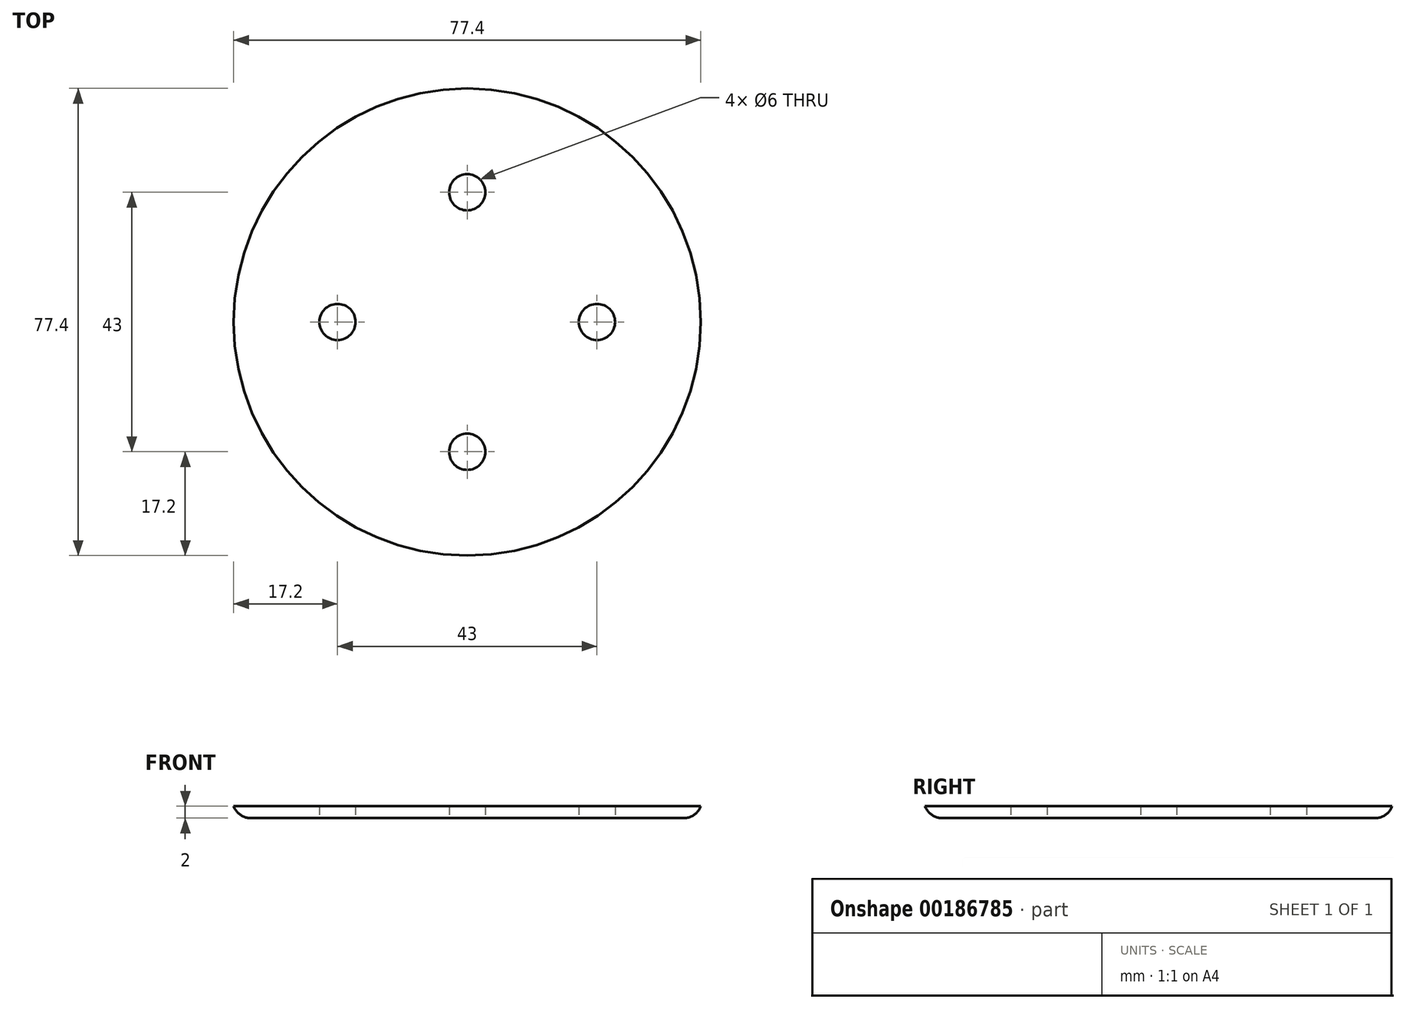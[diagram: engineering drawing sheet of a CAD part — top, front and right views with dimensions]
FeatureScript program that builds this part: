
annotation { "Feature Type Name" : "Feature", "Feature Type Description" : "" }
export const myFeature = defineFeature(function(context is Context, id is Id, definition is map)
    precondition{}
    {
        {
            var Q0;
            Q0=qCreatedBy(makeId("Top.planeOp"),FACE);
            var sketch = newSketch(context, id + "F0", { "sketchPlane" : qUnion([Q0])});
            skCircle(sketch, "E0", {"center": v(0, 0) * mm, "radius": 38.7 * mm});
            skLineSegment(sketch, "E1", {"start": v(-38.7, 0) * mm, "end": v(38.7, 0) * mm, "construction": true});
            skLineSegment(sketch, "E2", {"start": v(0, -38.7) * mm, "end": v(0, 38.7) * mm, "construction": true});
            skCircle(sketch, "E3", {"center": v(0, 21.5) * mm, "radius": 3 * mm});
            skCircle(sketch, "E4", {"center": v(21.5, 0) * mm, "radius": 3 * mm});
            skCircle(sketch, "E5", {"center": v(0, -21.5) * mm, "radius": 3 * mm});
            skCircle(sketch, "E6", {"center": v(-21.5, 0) * mm, "radius": 3 * mm});
            skSolve(sketch);
        }
        {
            var Q0;
            Q0 = qSketchRegion(id + "F0", true);
            extrude(context, id + "F1", {"entities" : qUnion([Q0]), "depth" : 2 * mm, "offsetDistance" : 25 * mm});
        }
        {
            var Q0;
            Q0=makeQuery(id+"F1.opExtrude","CAP_EDGE",EDGE,{"disambiguationData":[OSD([sQuery(id+"F0.wireOp",EDGE,"E0")])],"isStart":true});
            fillet(context, id + "F2", {"entities" : qUnion([Q0]), "radius" : 3 * mm, "tangentPropagation" : true, "allowEdgeOverflow" : false});
        }
    });
